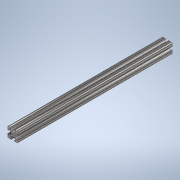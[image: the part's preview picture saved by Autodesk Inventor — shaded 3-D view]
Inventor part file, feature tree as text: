
AUTODESK INVENTOR PART (.ipt)
format: ipt  version: 2020 (Build 240168000, 168)  size: 239,616 bytes
history: native  units: in
note: dims shown in document units (in); Inventor stores cm internally (conversion verified against a paired STEP export)
features: extrude x1, sketch x1
ambient origin geometry x8: Origin, YZ Plane, XZ Plane, XY Plane, X Axis, Y Axis, Z Axis, Center Point
bodies: Solid1 (feature_tree)
feature tree (2):
  extrude  "Extrusion1"  [1 undecoded]
  sketch  "Sketch1"  dims[d0=15.0in d1=0.0in]
note: 1 required parameter value undecoded (feature->parameter linkage not recoverable at this tier; creation-order binding heuristic only, values carry confidence <= 0.55)
